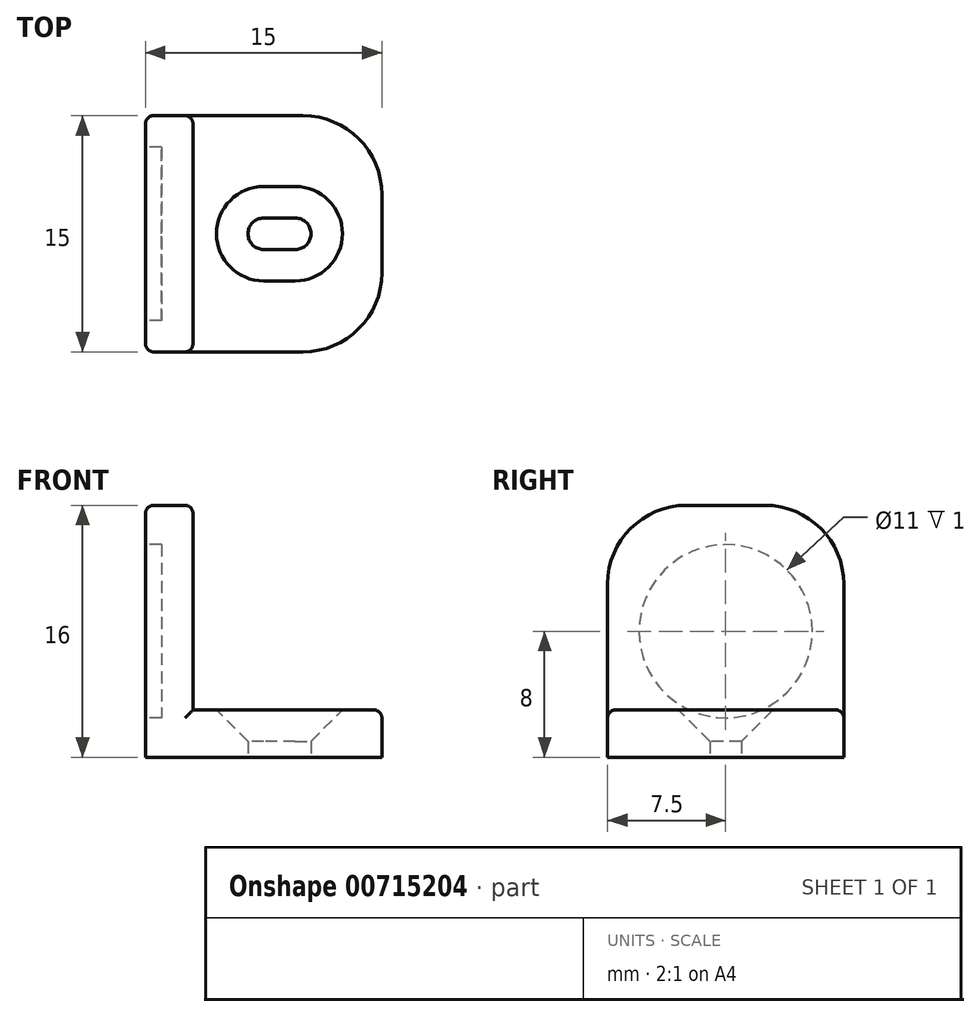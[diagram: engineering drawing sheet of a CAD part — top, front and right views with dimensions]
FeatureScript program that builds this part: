
annotation { "Feature Type Name" : "Feature", "Feature Type Description" : "" }
export const myFeature = defineFeature(function(context is Context, id is Id, definition is map)
    precondition{}
    {
        {
            var Q0;
            Q0=qCreatedBy(makeId("Top.planeOp"),FACE);
            var sketch = newSketch(context, id + "F0", { "sketchPlane" : qUnion([Q0])});
            skCircle(sketch, "E0", {"center": v(0, 0) * mm, "radius": 1 * mm});
            skLineSegment(sketch, "E1.bottom", {"start": v(-7.5, 7.5) * mm, "end": v(7.5, 7.5) * mm});
            skLineSegment(sketch, "E1.top", {"start": v(-7.5, -7.5) * mm, "end": v(7.5, -7.5) * mm});
            skLineSegment(sketch, "E1.left", {"start": v(-7.5, 7.5) * mm, "end": v(-7.5, -7.5) * mm});
            skLineSegment(sketch, "E1.right", {"start": v(7.5, 7.5) * mm, "end": v(7.5, -7.5) * mm});
            skLineSegment(sketch, "E2", {"start": v(-4.5, 7.5) * mm, "end": v(-4.5, -7.5) * mm});
            skLineSegment(sketch, "E3", {"start": v(0, 0) * mm, "end": v(2, 0) * mm, "construction": true});
            skCircle(sketch, "E4", {"center": v(2, 0) * mm, "radius": 1 * mm});
            skLineSegment(sketch, "E5", {"start": v(0, 1) * mm, "end": v(2, 1) * mm});
            skLineSegment(sketch, "E6", {"start": v(0, -1) * mm, "end": v(2, -1) * mm});
            skSolve(sketch);
        }
        {
            var Q0;
            {var subQ0=sQuery(id+"F0.wireOp",EDGE,"E1.left");Q0=makeQuery(id+"F0.imprint","IMPRINT",FACE,{"disambiguationData":[TD([[makeQuery(id+"F0.imprint","IMPRINT",EDGE,{"derivedFrom":subQ0}),1.0]])]});}
            extrude(context, id + "F1", {"entities" : qUnion([Q0]), "depth" : 16 * mm, "offsetDistance" : 25 * mm});
        }
        {
            var Q0;
            {var subQ0=sQuery(id+"F0.wireOp",EDGE,"E1.right");Q0=makeQuery(id+"F0.imprint","IMPRINT",FACE,{"disambiguationData":[TD([[makeQuery(id+"F0.imprint","IMPRINT",EDGE,{"derivedFrom":subQ0}),-1.0]])]});}
            extrude(context, id + "F2", {"entities" : qUnion([Q0]), "operationType" : NewBodyOperationType.ADD, "depth" : 3 * mm, "offsetDistance" : 25 * mm});
        }
        {
            var Q0;
            Q0=makeQuery(id+"F1.opExtrude","SWEPT_FACE",FACE,{"disambiguationData":[OSD([sQuery(id+"F0.wireOp",EDGE,"E1.left")])]});
            var sketch = newSketch(context, id + "F3", { "sketchPlane" : qUnion([Q0])});
            skCircle(sketch, "E7", {"center": v(0, 8) * mm, "radius": 5.5 * mm});
            skSolve(sketch);
        }
        {
            var Q0;
            Q0=makeQuery(id+"F3.imprint","IMPRINT",FACE,{"disambiguationData":[TD([[makeQuery(id+"F3.imprint","IMPRINT",EDGE,{"derivedFrom":sQuery(id+"F3.wireOp",EDGE,"E7")}),1.0]])]});
            extrude(context, id + "F4", {"entities" : qUnion([Q0]), "operationType" : NewBodyOperationType.REMOVE, "oppositeDirection" : true, "depth" : 1 * mm, "offsetDistance" : 25 * mm});
        }
        {
            var Q0;
            Q0=makeQuery(id+"F2.opExtrude","CAP_EDGE",EDGE,{"disambiguationData":[OSD([sQuery(id+"F0.wireOp",EDGE,"E0")])],"isStart":false});
            chamfer(context, id + "F5", {"entities" : qUnion([Q0]), "width" : 2 * mm, "tangentPropagation" : true});
        }
        {
            var Q0;
            Q0=makeQuery(id+"F1.opExtrude","CAP_EDGE",EDGE,{"disambiguationData":[OSD([sQuery(id+"F0.wireOp",EDGE,"E1.top")])],"isStart":false});
            var Q1;
            Q1=makeQuery(id+"F1.opExtrude","CAP_EDGE",EDGE,{"disambiguationData":[OSD([sQuery(id+"F0.wireOp",EDGE,"E1.bottom")])],"isStart":false});
            var Q2;
            Q2=makeQuery(id+"F2.opExtrude","SWEPT_EDGE",EDGE,{"disambiguationData":[OSD([sQuery(id+"F0.wireOp",EDGE,"E1.top"),sQuery(id+"F0.wireOp",EDGE,"E1.right")])]});
            var Q3;
            Q3=makeQuery(id+"F2.opExtrude","SWEPT_EDGE",EDGE,{"disambiguationData":[OSD([sQuery(id+"F0.wireOp",EDGE,"E1.bottom"),sQuery(id+"F0.wireOp",EDGE,"E1.right")])]});
            fillet(context, id + "F6", {"entities" : qUnion([Q0, Q1, Q2, Q3]), "radius" : 5 * mm, "tangentPropagation" : true, "allowEdgeOverflow" : false});
        }
        {
            var Q0;
            Q0=makeQuery(id+"F4.boolean.opBoolean","COPY",EDGE,{"derivedFrom":makeQuery(id+"F4.opExtrude","CAP_EDGE",EDGE,{"disambiguationData":[OSD([sQuery(id+"F3.wireOp",EDGE,"E7")])],"isStart":true})});
            var Q1;
            Q1=makeQuery(id+"F6.opFillet","BLEND_EDGE",EDGE,{"blendedFrom":[makeQuery(id+"F1.opExtrude","CAP_EDGE",EDGE,{"disambiguationData":[OSD([sQuery(id+"F0.wireOp",EDGE,"E1.bottom")])],"isStart":false}),makeQuery(id+"F1.opExtrude","SWEPT_FACE",FACE,{"disambiguationData":[OSD([sQuery(id+"F0.wireOp",EDGE,"E1.left")])]})],"blendedInto":[makeQuery(id+"F1.opExtrude","SWEPT_FACE",FACE,{"disambiguationData":[OSD([sQuery(id+"F0.wireOp",EDGE,"E1.left")])]})]});
            var Q2;
            Q2=makeQuery(id+"F6.opFillet","BLEND_EDGE",EDGE,{"blendedFrom":[makeQuery(id+"F1.opExtrude","CAP_EDGE",EDGE,{"disambiguationData":[OSD([sQuery(id+"F0.wireOp",EDGE,"E1.top")])],"isStart":false}),makeQuery(id+"F1.opExtrude","SWEPT_FACE",FACE,{"disambiguationData":[OSD([sQuery(id+"F0.wireOp",EDGE,"E2")])]})],"blendedInto":[makeQuery(id+"F1.opExtrude","SWEPT_FACE",FACE,{"disambiguationData":[OSD([sQuery(id+"F0.wireOp",EDGE,"E2")])]})]});
            var Q3;
            {var subQ0=sQuery(id+"F0.wireOp",EDGE,"E1.right");var subQ1=sQuery(id+"F0.wireOp",EDGE,"E1.top");Q3=makeQuery(id+"F6.opFillet","BLEND_EDGE",EDGE,{"blendedFrom":[makeQuery(id+"F2.opExtrude","SWEPT_EDGE",EDGE,{"disambiguationData":[OSD([subQ1,subQ0])]}),makeQuery(id+"F2.opExtrude","CAP_FACE",FACE,{"disambiguationData":[OSD([sQuery(id+"F0.wireOp",EDGE,"E0"),sQuery(id+"F0.wireOp",EDGE,"E1.bottom"),subQ1,subQ0,sQuery(id+"F0.wireOp",EDGE,"E2"),sQuery(id+"F0.wireOp",EDGE,"E4"),sQuery(id+"F0.wireOp",EDGE,"E5"),sQuery(id+"F0.wireOp",EDGE,"E6")])],"isStart":false})],"blendedInto":[makeQuery(id+"F2.opExtrude","CAP_FACE",FACE,{"disambiguationData":[OSD([sQuery(id+"F0.wireOp",EDGE,"E0"),sQuery(id+"F0.wireOp",EDGE,"E1.bottom"),subQ1,subQ0,sQuery(id+"F0.wireOp",EDGE,"E2"),sQuery(id+"F0.wireOp",EDGE,"E4"),sQuery(id+"F0.wireOp",EDGE,"E5"),sQuery(id+"F0.wireOp",EDGE,"E6")])],"isStart":false})]});}
            fillet(context, id + "F7", {"entities" : qUnion([Q0, Q1, Q2, Q3]), "radius" : 0.5 * mm, "tangentPropagation" : true, "allowEdgeOverflow" : false});
        }
    });
